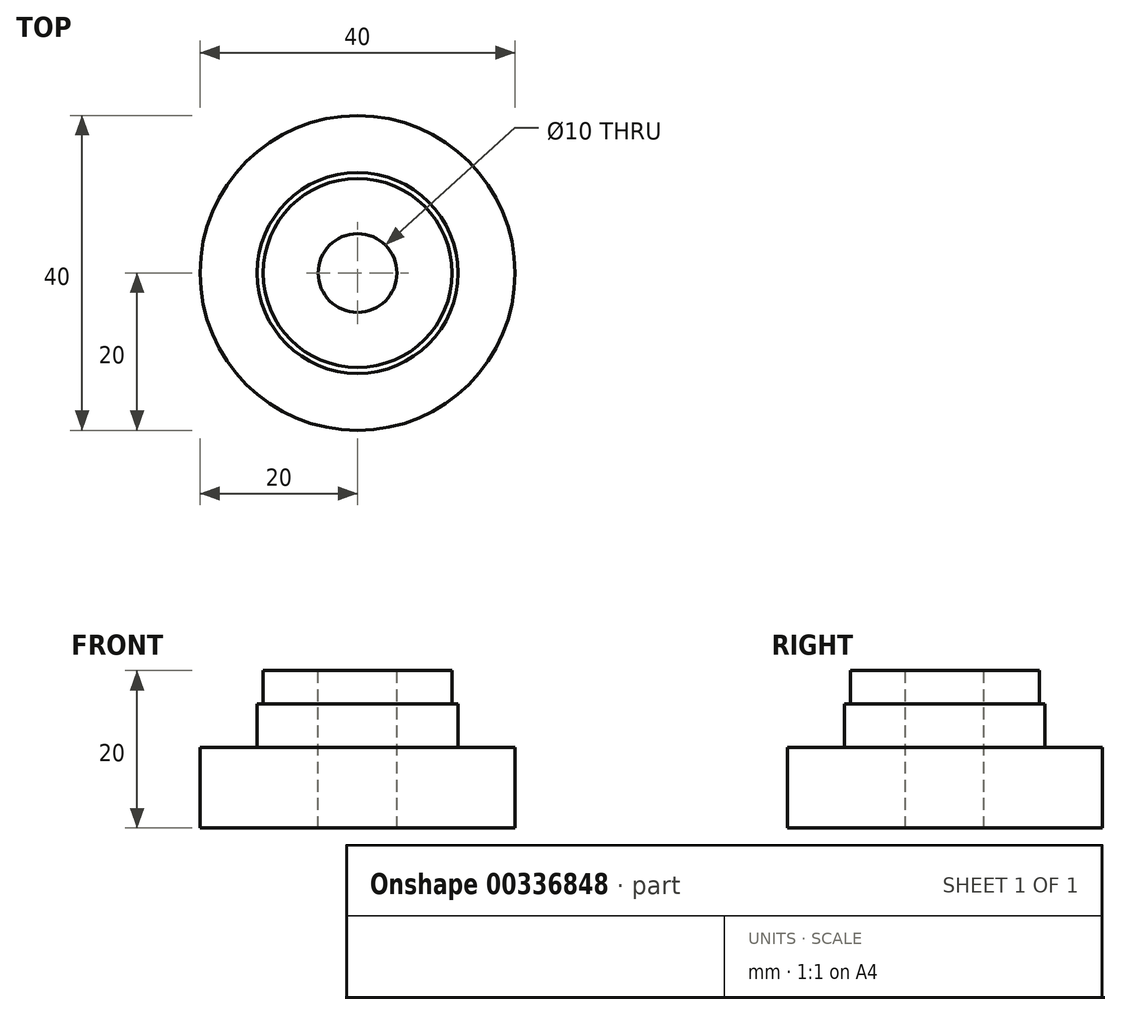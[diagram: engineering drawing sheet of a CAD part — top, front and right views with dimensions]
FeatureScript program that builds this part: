
annotation { "Feature Type Name" : "Feature", "Feature Type Description" : "" }
export const myFeature = defineFeature(function(context is Context, id is Id, definition is map)
    precondition{}
    {
        {
            var Q0;
            Q0=qCreatedBy(makeId("Top.planeOp"),FACE);
            var sketch = newSketch(context, id + "F0", { "sketchPlane" : qUnion([Q0])});
            skCircle(sketch, "E0", {"center": v(0, 0) * mm, "radius": 20 * mm});
            skSolve(sketch);
        }
        {
            var Q0;
            Q0 = qSketchRegion(id + "F0", true);
            extrude(context, id + "F1", {"entities" : qUnion([Q0]), "depth" : 6 * mm});
        }
        {
            var Q0;
            Q0=makeQuery(id+"F1.opExtrude","CAP_FACE",FACE,{"disambiguationData":[OSD([sQuery(id+"F0.wireOp",EDGE,"E0")])],"isStart":false});
            extrude(context, id + "F2", {"entities" : qUnion([Q0]), "operationType" : NewBodyOperationType.ADD, "depth" : 4.25 * mm});
        }
        {
            var Q0;
            Q0=makeQuery(id+"F2.opExtrude","CAP_FACE",FACE,{"disambiguationData":[OSD([sQuery(id+"F0.wireOp",EDGE,"E0")])],"isStart":false});
            var sketch = newSketch(context, id + "F3", { "sketchPlane" : qUnion([Q0])});
            skCircle(sketch, "E1", {"center": v(0, 0) * mm, "radius": 12.75 * mm});
            skSolve(sketch);
        }
        {
            var Q0;
            Q0 = qSketchRegion(id + "F3", true);
            extrude(context, id + "F4", {"entities" : qUnion([Q0]), "operationType" : NewBodyOperationType.ADD, "depth" : 5.5 * mm});
        }
        {
            var Q0;
            Q0=makeQuery(id+"F4.opExtrude","CAP_FACE",FACE,{"disambiguationData":[OSD([sQuery(id+"F3.wireOp",EDGE,"E1")])],"isStart":false});
            var sketch = newSketch(context, id + "F5", { "sketchPlane" : qUnion([Q0])});
            skCircle(sketch, "E2", {"center": v(0, 0) * mm, "radius": 12 * mm});
            skSolve(sketch);
        }
        {
            var Q0;
            Q0 = qSketchRegion(id + "F5", true);
            extrude(context, id + "F6", {"entities" : qUnion([Q0]), "operationType" : NewBodyOperationType.ADD, "depth" : 4.25 * mm});
        }
        {
            var Q0;
            Q0=makeQuery(id+"F6.opExtrude","CAP_FACE",FACE,{"disambiguationData":[OSD([sQuery(id+"F5.wireOp",EDGE,"E2")])],"isStart":false});
            var sketch = newSketch(context, id + "F7", { "sketchPlane" : qUnion([Q0])});
            skCircle(sketch, "E3", {"center": v(0, 0) * mm, "radius": 5 * mm});
            skSolve(sketch);
        }
        {
            var Q0;
            Q0 = qSketchRegion(id + "F7", true);
            extrude(context, id + "F8", {"entities" : qUnion([Q0]), "operationType" : NewBodyOperationType.REMOVE, "endBound" : BoundingType.THROUGH_ALL, "depth" : 0 * mm});
        }
        {
            var Q0;
            Q0 = qSketchRegion(id + "F7", true);
            extrude(context, id + "F9", {"entities" : qUnion([Q0]), "operationType" : NewBodyOperationType.REMOVE, "endBound" : BoundingType.THROUGH_ALL, "oppositeDirection" : true, "depth" : 25 * mm});
        }
    });
